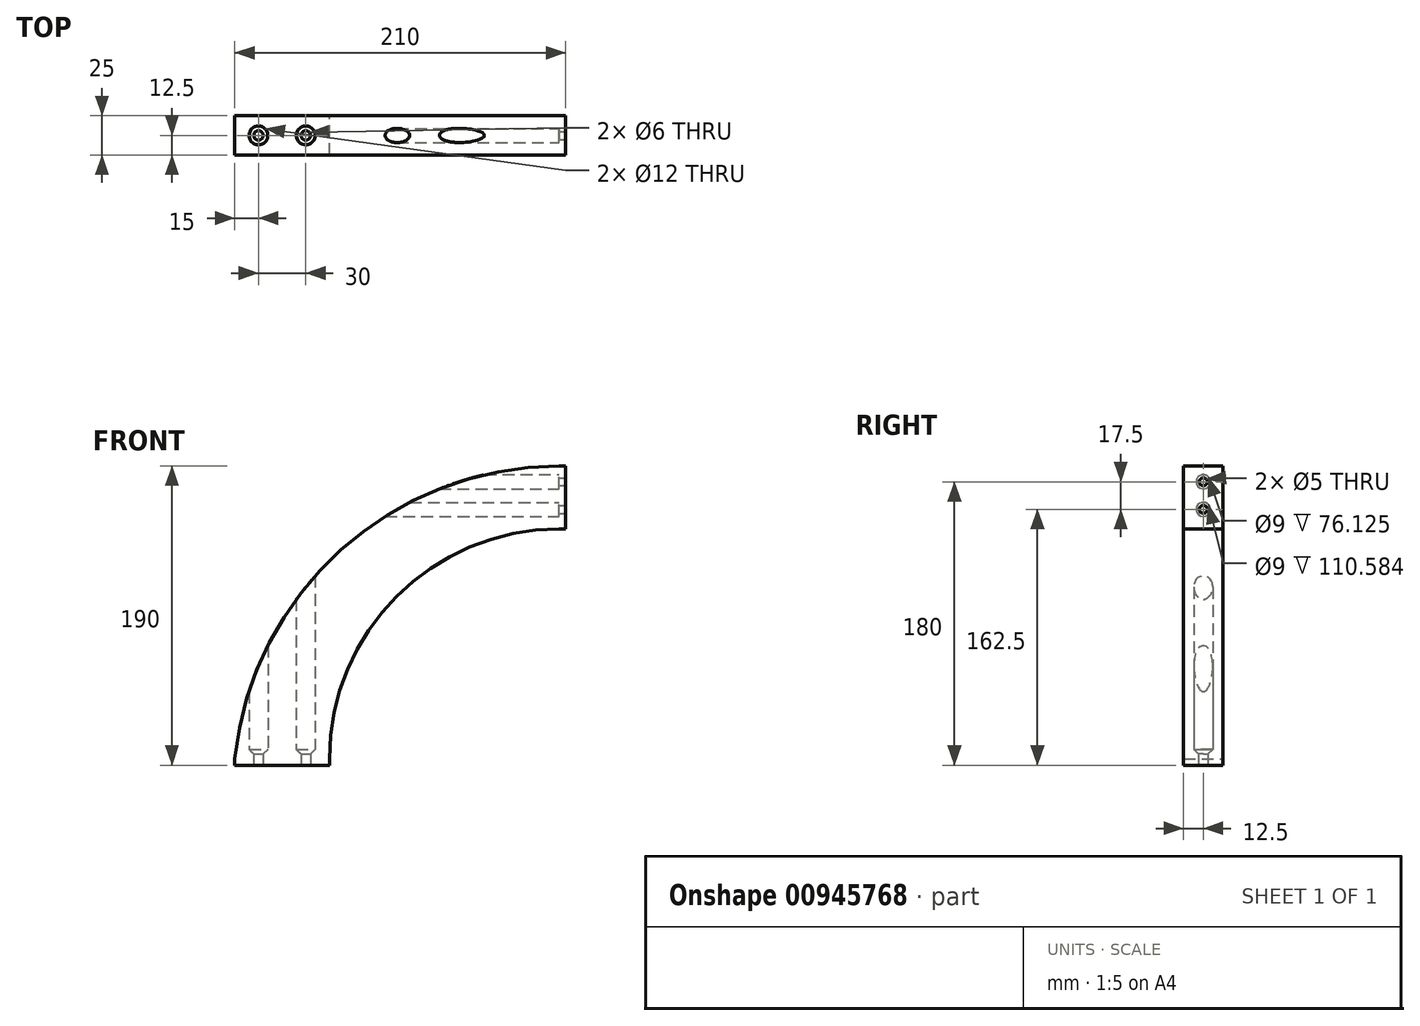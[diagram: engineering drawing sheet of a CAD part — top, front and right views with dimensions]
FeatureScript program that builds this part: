
annotation { "Feature Type Name" : "Feature", "Feature Type Description" : "" }
export const myFeature = defineFeature(function(context is Context, id is Id, definition is map)
    precondition{}
    {
        {
            var Q0;
            Q0=qCreatedBy(makeId("Front.planeOp"),FACE);
            var sketch = newSketch(context, id + "F0", { "sketchPlane" : qUnion([Q0])});
            skLineSegment(sketch, "E0.bottom", {"start": v(0, 190) * mm, "end": v(-4, 190) * mm});
            skLineSegment(sketch, "E0.top", {"start": v(0, 150) * mm, "end": v(-4, 150) * mm});
            skLineSegment(sketch, "E0.left", {"start": v(0, 190) * mm, "end": v(0, 150) * mm});
            skLineSegment(sketch, "E1.bottom", {"start": v(-210, 0) * mm, "end": v(-150, 0) * mm});
            skLineSegment(sketch, "E1.left", {"start": v(-210, 0) * mm, "end": v(-210, 4) * mm});
            skLineSegment(sketch, "E1.right", {"start": v(-150, 0) * mm, "end": v(-150, 4) * mm});
            skArc(sketch, "E2", {"start": v(-4, 190) * mm, "mid": v(-142.77, 136.62) * mm, "end": v(-210, 4) * mm});
            skArc(sketch, "E3", {"start": v(-4, 150) * mm, "mid": v(-107.24, 107.24) * mm, "end": v(-150, 4) * mm});
            skSolve(sketch);
        }
        {
            var Q0;
            Q0 = qSketchRegion(id + "F0", true);
            extrude(context, id + "F1", {"entities" : qUnion([Q0]), "endBound" : BoundingType.SYMMETRIC, "depth" : 25 * mm, "offsetDistance" : 25 * mm});
        }
        {
            var Q0;
            Q0=makeQuery(id+"F1.opExtrude","SWEPT_FACE",FACE,{"disambiguationData":[OSD([sQuery(id+"F0.wireOp",EDGE,"E0.left")])]});
            var sketch = newSketch(context, id + "F2", { "sketchPlane" : qUnion([Q0])});
            skCircle(sketch, "E4", {"center": v(0, 180) * mm, "radius": 2.5 * mm});
            skCircle(sketch, "E5", {"center": v(0, 162.5) * mm, "radius": 2.5 * mm});
            skPoint(sketch, "E6", {"position": v(0, 150) * mm});
            skSolve(sketch);
        }
        {
            var Q0;
            Q0 = qSketchRegion(id + "F2", true);
            extrude(context, id + "F3", {"entities" : qUnion([Q0]), "operationType" : NewBodyOperationType.REMOVE, "oppositeDirection" : true, "depth" : 4 * mm, "offsetDistance" : 25 * mm});
        }
        {
            var Q0;
            Q0=makeQuery(id+"F3.boolean.opBoolean","COPY",FACE,{"derivedFrom":makeQuery(id+"F3.opExtrude","CAP_FACE",FACE,{"disambiguationData":[OSD([sQuery(id+"F2.wireOp",EDGE,"E4")])],"isStart":false})});
            var sketch = newSketch(context, id + "F4", { "sketchPlane" : qUnion([Q0])});
            skCircle(sketch, "E7", {"center": v(0, 180) * mm, "radius": 4.5 * mm});
            skCircle(sketch, "E8", {"center": v(0, 162.5) * mm, "radius": 4.5 * mm});
            skSolve(sketch);
        }
        {
            var Q0;
            Q0 = qSketchRegion(id + "F4", true);
            extrude(context, id + "F5", {"entities" : qUnion([Q0]), "operationType" : NewBodyOperationType.REMOVE, "endBound" : BoundingType.THROUGH_ALL, "oppositeDirection" : true, "depth" : 25 * mm, "offsetDistance" : 25 * mm});
        }
        {
            var Q0;
            Q0=makeQuery(id+"F1.opExtrude","SWEPT_FACE",FACE,{"disambiguationData":[OSD([sQuery(id+"F0.wireOp",EDGE,"E1.bottom")])]});
            var sketch = newSketch(context, id + "F6", { "sketchPlane" : qUnion([Q0])});
            skCircle(sketch, "E9", {"center": v(-165, 0) * mm, "radius": 3 * mm});
            skCircle(sketch, "E10", {"center": v(-195, 0) * mm, "radius": 3 * mm});
            skSolve(sketch);
        }
        {
            var Q0;
            Q0 = qSketchRegion(id + "F6", true);
            extrude(context, id + "F7", {"entities" : qUnion([Q0]), "operationType" : NewBodyOperationType.REMOVE, "oppositeDirection" : true, "depth" : 5 * mm, "offsetDistance" : 25 * mm});
        }
        {
            var Q0;
            Q0=makeQuery(id+"F7.boolean.opBoolean","COPY",FACE,{"derivedFrom":makeQuery(id+"F7.opExtrude","CAP_FACE",FACE,{"disambiguationData":[OSD([sQuery(id+"F6.wireOp",EDGE,"E9")])],"isStart":false})});
            var sketch = newSketch(context, id + "F8", { "sketchPlane" : qUnion([Q0])});
            skCircle(sketch, "E11", {"center": v(-165, 0) * mm, "radius": 6 * mm});
            skCircle(sketch, "E12", {"center": v(-195, 0) * mm, "radius": 6 * mm});
            skSolve(sketch);
        }
        {
            var Q0;
            Q0 = qSketchRegion(id + "F8", true);
            extrude(context, id + "F9", {"entities" : qUnion([Q0]), "operationType" : NewBodyOperationType.REMOVE, "endBound" : BoundingType.THROUGH_ALL, "oppositeDirection" : true, "depth" : 25 * mm, "offsetDistance" : 25 * mm});
        }
        {
            var Q0;
            Q0=makeQuery(id+"F9.boolean.opBoolean","COPY",EDGE,{"derivedFrom":makeQuery(id+"F9.opExtrude","CAP_EDGE",EDGE,{"disambiguationData":[OSD([sQuery(id+"F8.wireOp",EDGE,"E12")])],"isStart":true})});
            var Q1;
            Q1=makeQuery(id+"F9.boolean.opBoolean","COPY",EDGE,{"derivedFrom":makeQuery(id+"F9.opExtrude","CAP_EDGE",EDGE,{"disambiguationData":[OSD([sQuery(id+"F8.wireOp",EDGE,"E11")])],"isStart":true})});
            chamfer(context, id + "F10", {"entities" : qUnion([Q0, Q1]), "width" : 5 * mm, "tangentPropagation" : true});
        }
    });
